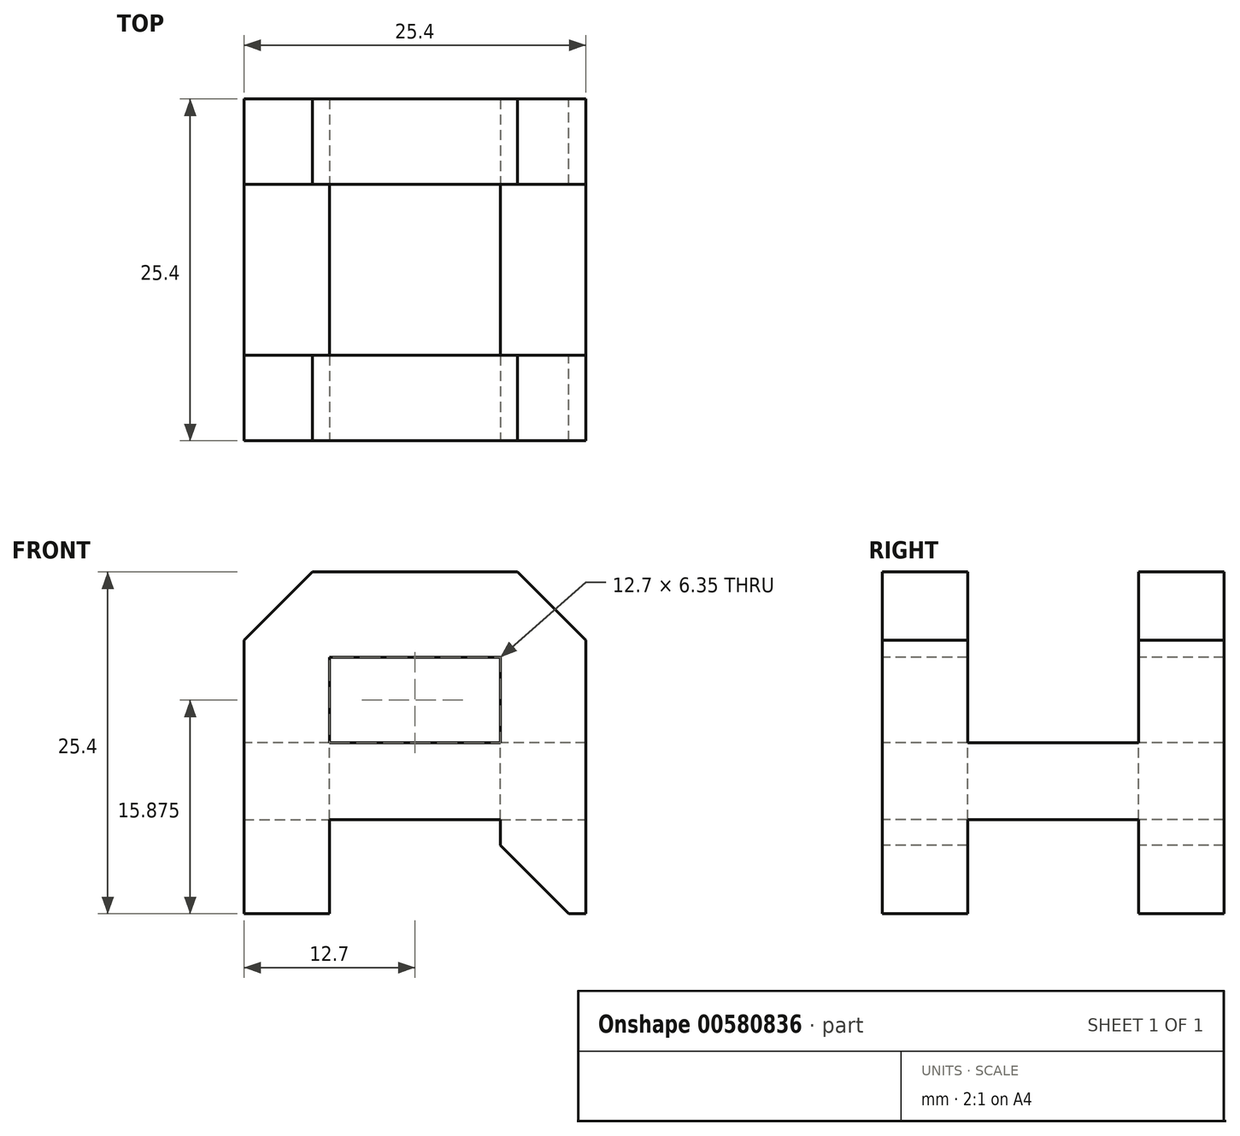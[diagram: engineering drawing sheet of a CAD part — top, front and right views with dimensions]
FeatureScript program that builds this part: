
annotation { "Feature Type Name" : "Feature", "Feature Type Description" : "" }
export const myFeature = defineFeature(function(context is Context, id is Id, definition is map)
    precondition{}
    {
        {
            var Q0;
            Q0=qCreatedBy(makeId("Front.planeOp"),FACE);
            var sketch = newSketch(context, id + "F0", { "sketchPlane" : qUnion([Q0])});
            skLineSegment(sketch, "E0.bottom", {"start": v(-12.7, 12.7) * mm, "end": v(12.7, 12.7) * mm});
            skLineSegment(sketch, "E0.top", {"start": v(-12.7, -12.7) * mm, "end": v(12.7, -12.7) * mm});
            skLineSegment(sketch, "E0.left", {"start": v(-12.7, 12.7) * mm, "end": v(-12.7, -12.7) * mm});
            skLineSegment(sketch, "E0.right", {"start": v(12.7, 12.7) * mm, "end": v(12.7, -12.7) * mm});
            skPoint(sketch, "E0.middle", {"position": v(0, 0) * mm});
            skSolve(sketch);
        }
        {
            var Q0;
            Q0 = qSketchRegion(id + "F0", true);
            extrude(context, id + "F1", {"entities" : qUnion([Q0]), "depth" : 25.4 * mm, "offsetDistance" : 25.4 * mm});
        }
        {
            var Q0;
            Q0=makeQuery(id+"F1.opExtrude","CAP_FACE",FACE,{"disambiguationData":[OSD([sQuery(id+"F0.wireOp",EDGE,"E0.bottom"),sQuery(id+"F0.wireOp",EDGE,"E0.top"),sQuery(id+"F0.wireOp",EDGE,"E0.left"),sQuery(id+"F0.wireOp",EDGE,"E0.right")])],"isStart":false});
            var sketch = newSketch(context, id + "F2", { "sketchPlane" : qUnion([Q0])});
            skLineSegment(sketch, "E1.bottom", {"start": v(-6.35, -12.7) * mm, "end": v(6.35, -12.7) * mm});
            skLineSegment(sketch, "E1.top", {"start": v(-6.35, -5.72) * mm, "end": v(6.35, -5.72) * mm});
            skLineSegment(sketch, "E1.left", {"start": v(-6.35, -12.7) * mm, "end": v(-6.35, -5.72) * mm});
            skLineSegment(sketch, "E1.right", {"start": v(6.35, -12.7) * mm, "end": v(6.35, -5.72) * mm});
            skLineSegment(sketch, "E2.bottom", {"start": v(-6.35, 6.35) * mm, "end": v(6.35, 6.35) * mm});
            skLineSegment(sketch, "E2.top", {"start": v(-6.35, 0) * mm, "end": v(6.35, 0) * mm});
            skLineSegment(sketch, "E2.left", {"start": v(-6.35, 6.35) * mm, "end": v(-6.35, 0) * mm});
            skLineSegment(sketch, "E2.right", {"start": v(6.35, 6.35) * mm, "end": v(6.35, 0) * mm});
            skSolve(sketch);
        }
        {
            var Q0;
            Q0 = qSketchRegion(id + "F2", true);
            extrude(context, id + "F3", {"entities" : qUnion([Q0]), "operationType" : NewBodyOperationType.REMOVE, "endBound" : BoundingType.THROUGH_ALL, "oppositeDirection" : true, "depth" : 25.4 * mm, "offsetDistance" : 25.4 * mm});
        }
        {
            var Q0;
            Q0=makeQuery(id+"F1.opExtrude","SWEPT_FACE",FACE,{"disambiguationData":[OSD([sQuery(id+"F0.wireOp",EDGE,"E0.left")])]});
            var sketch = newSketch(context, id + "F4", { "sketchPlane" : qUnion([Q0])});
            skLineSegment(sketch, "E3.bottom", {"start": v(6.35, 12.7) * mm, "end": v(19.05, 12.7) * mm});
            skLineSegment(sketch, "E3.top", {"start": v(6.35, 0) * mm, "end": v(19.05, 0) * mm});
            skLineSegment(sketch, "E3.left", {"start": v(6.35, 12.7) * mm, "end": v(6.35, 0) * mm});
            skLineSegment(sketch, "E3.right", {"start": v(19.05, 12.7) * mm, "end": v(19.05, 0) * mm});
            skSolve(sketch);
        }
        {
            var Q0;
            Q0 = qSketchRegion(id + "F4", true);
            extrude(context, id + "F5", {"entities" : qUnion([Q0]), "operationType" : NewBodyOperationType.REMOVE, "endBound" : BoundingType.THROUGH_ALL, "oppositeDirection" : true, "depth" : 25.4 * mm, "offsetDistance" : 25.4 * mm});
        }
        {
            var Q0;
            Q0=makeQuery(id+"F1.opExtrude","SWEPT_FACE",FACE,{"disambiguationData":[OSD([sQuery(id+"F0.wireOp",EDGE,"E0.right")])]});
            var sketch = newSketch(context, id + "F6", { "sketchPlane" : qUnion([Q0])});
            skLineSegment(sketch, "E4.bottom", {"start": v(-19.05, -12.7) * mm, "end": v(-6.35, -12.7) * mm});
            skLineSegment(sketch, "E4.top", {"start": v(-19.05, -5.72) * mm, "end": v(-6.35, -5.72) * mm});
            skLineSegment(sketch, "E4.left", {"start": v(-19.05, -12.7) * mm, "end": v(-19.05, -5.72) * mm});
            skLineSegment(sketch, "E4.right", {"start": v(-6.35, -12.7) * mm, "end": v(-6.35, -5.72) * mm});
            skSolve(sketch);
        }
        {
            var Q0;
            Q0 = qSketchRegion(id + "F6", true);
            extrude(context, id + "F7", {"entities" : qUnion([Q0]), "operationType" : NewBodyOperationType.REMOVE, "endBound" : BoundingType.THROUGH_ALL, "oppositeDirection" : true, "depth" : 25.4 * mm, "offsetDistance" : 25.4 * mm});
        }
        {
            var Q0;
            Q0=makeQuery(id+"F5.boolean.opBoolean","MERGE",FACE,{"derivedFrom":[makeQuery(id+"F3.boolean.opBoolean","COPY",FACE,{"derivedFrom":makeQuery(id+"F3.opExtrude","SWEPT_FACE",FACE,{"disambiguationData":[OSD([sQuery(id+"F2.wireOp",EDGE,"E2.top")])]})}),makeQuery(id+"F5.opExtrude","SWEPT_FACE",FACE,{"disambiguationData":[OSD([sQuery(id+"F4.wireOp",EDGE,"E3.top")])]})]});
            var sketch = newSketch(context, id + "F8", { "sketchPlane" : qUnion([Q0])});
            skLineSegment(sketch, "E5.bottom", {"start": v(-6.35, -19.05) * mm, "end": v(6.35, -19.05) * mm});
            skLineSegment(sketch, "E5.top", {"start": v(-6.35, -6.35) * mm, "end": v(6.35, -6.35) * mm});
            skLineSegment(sketch, "E5.left", {"start": v(-6.35, -19.05) * mm, "end": v(-6.35, -6.35) * mm});
            skLineSegment(sketch, "E5.right", {"start": v(6.35, -19.05) * mm, "end": v(6.35, -6.35) * mm});
            skSolve(sketch);
        }
        {
            var Q0;
            Q0 = qSketchRegion(id + "F8", true);
            extrude(context, id + "F9", {"entities" : qUnion([Q0]), "operationType" : NewBodyOperationType.REMOVE, "endBound" : BoundingType.THROUGH_ALL, "oppositeDirection" : true, "depth" : 25.4 * mm, "offsetDistance" : 25.4 * mm});
        }
        {
            var Q0;
            {var subQ0=sQuery(id+"F0.wireOp",EDGE,"E0.top");var subQ1=sQuery(id+"F2.wireOp",EDGE,"E1.right");Q0=makeQuery(id+"F7.boolean.opBoolean","SPLIT",EDGE,{"disambiguationData":[TD([makeQuery(id+"F7.opExtrude","SWEPT_FACE",FACE,{"disambiguationData":[OSD([sQuery(id+"F6.wireOp",EDGE,"E4.left")])]})])],"derivedFrom":makeQuery(id+"F3.boolean.opBoolean","COPY",EDGE,{"derivedFrom":makeQuery(id+"F3.opExtrude","SWEPT_EDGE",EDGE,{"disambiguationData":[OSD([subQ0,sQuery(id+"F2.wireOp",EDGE,"E1.bottom"),subQ1])]})})});}
            var Q1;
            {var subQ0=sQuery(id+"F0.wireOp",EDGE,"E0.top");var subQ1=sQuery(id+"F2.wireOp",EDGE,"E1.right");Q1=makeQuery(id+"F7.boolean.opBoolean","SPLIT",EDGE,{"disambiguationData":[TD([makeQuery(id+"F7.opExtrude","SWEPT_FACE",FACE,{"disambiguationData":[OSD([sQuery(id+"F6.wireOp",EDGE,"E4.right")])]})])],"derivedFrom":makeQuery(id+"F3.boolean.opBoolean","COPY",EDGE,{"derivedFrom":makeQuery(id+"F3.opExtrude","SWEPT_EDGE",EDGE,{"disambiguationData":[OSD([subQ0,sQuery(id+"F2.wireOp",EDGE,"E1.bottom"),subQ1])]})})});}
            var Q2;
            {var subQ0=sQuery(id+"F0.wireOp",EDGE,"E0.top");var subQ1=sQuery(id+"F2.wireOp",EDGE,"E1.left");Q2=makeQuery(id+"F7.boolean.opBoolean","SPLIT",EDGE,{"disambiguationData":[TD([makeQuery(id+"F7.opExtrude","SWEPT_FACE",FACE,{"disambiguationData":[OSD([sQuery(id+"F6.wireOp",EDGE,"E4.right")])]})])],"derivedFrom":makeQuery(id+"F3.boolean.opBoolean","COPY",EDGE,{"derivedFrom":makeQuery(id+"F3.opExtrude","SWEPT_EDGE",EDGE,{"disambiguationData":[OSD([subQ0,sQuery(id+"F2.wireOp",EDGE,"E1.bottom"),subQ1])]})})});}
            var Q3;
            {var subQ0=sQuery(id+"F0.wireOp",EDGE,"E0.top");var subQ1=sQuery(id+"F2.wireOp",EDGE,"E1.left");Q3=makeQuery(id+"F7.boolean.opBoolean","SPLIT",EDGE,{"disambiguationData":[TD([makeQuery(id+"F7.opExtrude","SWEPT_FACE",FACE,{"disambiguationData":[OSD([sQuery(id+"F6.wireOp",EDGE,"E4.left")])]})])],"derivedFrom":makeQuery(id+"F3.boolean.opBoolean","COPY",EDGE,{"derivedFrom":makeQuery(id+"F3.opExtrude","SWEPT_EDGE",EDGE,{"disambiguationData":[OSD([subQ0,sQuery(id+"F2.wireOp",EDGE,"E1.bottom"),subQ1])]})})});}
            var Q4;
            {var subQ0=sQuery(id+"F0.wireOp",EDGE,"E0.bottom");var subQ1=sQuery(id+"F0.wireOp",EDGE,"E0.right");Q4=makeQuery(id+"F5.boolean.opBoolean","SPLIT",EDGE,{"disambiguationData":[TD([makeQuery(id+"F5.opExtrude","SWEPT_FACE",FACE,{"disambiguationData":[OSD([sQuery(id+"F4.wireOp",EDGE,"E3.left")])]})])],"derivedFrom":makeQuery(id+"F1.opExtrude","SWEPT_EDGE",EDGE,{"disambiguationData":[OSD([subQ0,subQ1])]})});}
            var Q5;
            {var subQ0=sQuery(id+"F0.wireOp",EDGE,"E0.bottom");var subQ1=sQuery(id+"F0.wireOp",EDGE,"E0.right");Q5=makeQuery(id+"F5.boolean.opBoolean","SPLIT",EDGE,{"disambiguationData":[TD([makeQuery(id+"F5.opExtrude","SWEPT_FACE",FACE,{"disambiguationData":[OSD([sQuery(id+"F4.wireOp",EDGE,"E3.right")])]})])],"derivedFrom":makeQuery(id+"F1.opExtrude","SWEPT_EDGE",EDGE,{"disambiguationData":[OSD([subQ0,subQ1])]})});}
            var Q6;
            {var subQ0=sQuery(id+"F0.wireOp",EDGE,"E0.bottom");var subQ1=sQuery(id+"F0.wireOp",EDGE,"E0.left");Q6=makeQuery(id+"F5.boolean.opBoolean","SPLIT",EDGE,{"disambiguationData":[TD([makeQuery(id+"F5.opExtrude","SWEPT_FACE",FACE,{"disambiguationData":[OSD([sQuery(id+"F4.wireOp",EDGE,"E3.right")])]})])],"derivedFrom":makeQuery(id+"F1.opExtrude","SWEPT_EDGE",EDGE,{"disambiguationData":[OSD([subQ0,subQ1])]})});}
            var Q7;
            {var subQ0=sQuery(id+"F0.wireOp",EDGE,"E0.bottom");var subQ1=sQuery(id+"F0.wireOp",EDGE,"E0.left");Q7=makeQuery(id+"F5.boolean.opBoolean","SPLIT",EDGE,{"disambiguationData":[TD([makeQuery(id+"F5.opExtrude","SWEPT_FACE",FACE,{"disambiguationData":[OSD([sQuery(id+"F4.wireOp",EDGE,"E3.left")])]})])],"derivedFrom":makeQuery(id+"F1.opExtrude","SWEPT_EDGE",EDGE,{"disambiguationData":[OSD([subQ0,subQ1])]})});}
            chamfer(context, id + "F10", {"entities" : qUnion([Q0, Q1, Q2, Q3, Q4, Q5, Q6, Q7]), "width" : 5.08 * mm, "tangentPropagation" : true});
        }
    });
